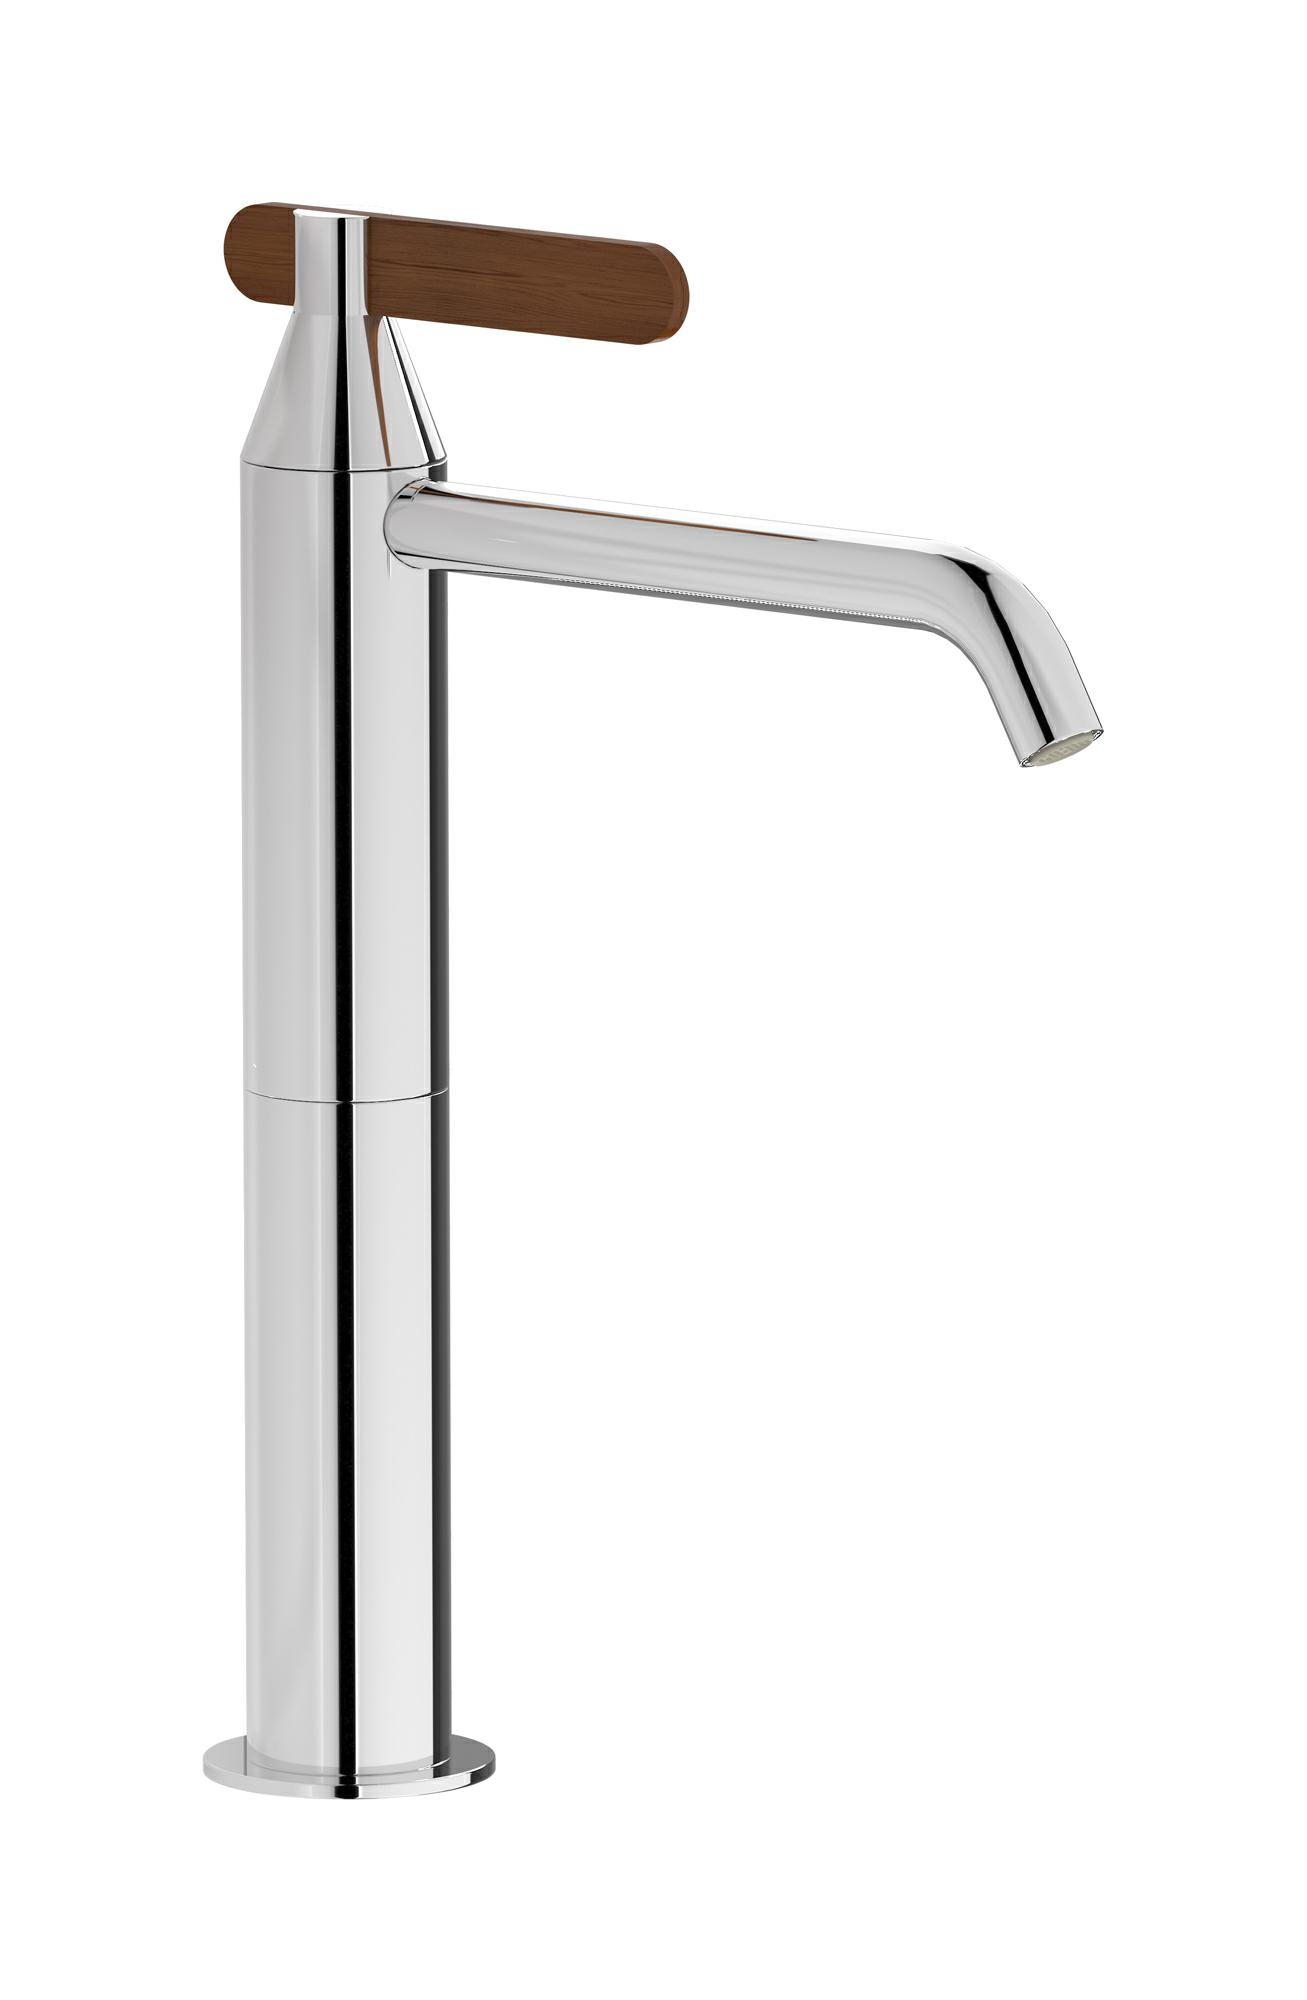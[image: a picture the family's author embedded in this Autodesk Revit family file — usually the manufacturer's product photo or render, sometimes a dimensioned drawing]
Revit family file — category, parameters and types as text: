
# Revit family: OL370
name_source: partatom
category: Apparecchi idraulici
units: mm (PartAtom-declared; Revit-internal decimal feet)

## family parameters
Basato su piano di lavoro = No
Condiviso = No
Mantieni orientamento annotazione = No
Numero OmniClass = 23.45.55.17
Punto di calcolo locali = No
Quota connettore circolare = Usa diametro
Sempre verticale = Sì
Taglio con vuoti quando caricato = No
Tipo di parte = Normale
Titolo OmniClass = Mixing Faucets

## types (6) — shared parameters
Cold water inlet = 10 mm  [stored 0.0328084 ft]
Commenti sul tipo = Single lever kitchen mixer
Connessione CW = No
Connessione HW = No
Connessione di scarico = No
Connessione di ventilazione = No
Descrizione = Single lever kitchen mixer
Hot water inlet = 10 mm  [stored 0.0328084 ft]
Produttore = IB Rubinetterie S.p.A.
URL = https://www.weareib.it
zero-valued in all types: Prospetto di default

## per-type parameters (varying)
| type | Finishes surface | Immagine tipo | Modello |
| Chrome | IB_Chrome | OL370CC.jpg | OL370CC |
| Brushed Black Chrome | IB_Brushed black chrome | OL370CS.jpg | OL370CS |
| Brushed Pale Gold | IB_brushed pale gold | OL370IS.jpg | OL370IS |
| Natural Brass | IB_Brass | OL370ON.jpg | OL370ON |
| Brushed Rose Gold | IB_Brushed rose gold | OL370SR.jpg | OL370SR |
| Brushed Nickel | IB_Brushed nickel | OL370SS.jpg | OL370SS |

note: [stored X ft] marks values corroborated as IEEE doubles in the binary element streams (Revit-internal decimal feet)
